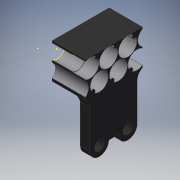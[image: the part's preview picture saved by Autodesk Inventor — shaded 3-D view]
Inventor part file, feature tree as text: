
AUTODESK INVENTOR PART (.ipt)
format: ipt  version: 2016 (Build 200138000, 138)  size: 355,328 bytes
history: native  units: in
note: dims shown in document units (in); Inventor stores cm internally (conversion verified against a paired STEP export)
features: sketch x6, extrude x5, other x3, projected_geometry x1, reference x1
ambient origin geometry x8: Origin, YZ Plane, XZ Plane, XY Plane, X Axis, Y Axis, Z Axis, Center Point
bodies: Body1 (feature_tree)
feature tree (16):
  other  "motor holders.ipt"
  extrude  "Extrusion1"  Depth=0.4331in
  sketch  "Sketch3"  dims[d3=0.1575in d4=0.1575in]
  extrude  "Extrusion2"  Depth=0.1575in
  extrude  "Extrusion3"  Depth=0.1575in
  extrude  "Extrusion4"  Depth=1.0in TaperAngle=0.0deg
  extrude  "Extrusion5"  Depth=1.0in TaperAngle=0.0deg
  other  "Solid2::motor holders.ipt"
  other  "TaggingFeature2"
  sketch  "Sketch2"  dims[d1=0.4331in d2=0.1575in]
  projected_geometry  "Projected Loop1"
  sketch  "Sketch4"  dims[d5=0.1575in d6=0.1575in]
  reference  "Reference1"
  sketch  "Sketch5"  dims[d7=0.1575in d8=1.0in d9=0.0in]
  sketch  "Sketch6"  dims[d10=0.1575in d11=1.0in d12=0.0in]
  sketch  "Sketch7"  dims[d13=0.1575in d14=1.0in d15=0.0in d16=0.1654in d17=0.1654in d18=0.1654in d19=0.1693in d20=0.1693in d21=0.1654in d22=0.1654in d23=0.1181in d24=0.0in d25=0.0472in d28=0.0553in d29=0.0553in d30=0.0553in d34=0.0787in d35=0.0in]
